# Revit family: Zumtobel MIRLRO NIV M600Q
name_source: partatom
category: Leuchten
revit_build: Autodesk Revit 2016 (Build: 20150714_1515(x64)
units: mm (PartAtom-declared; Revit-internal decimal feet)

## family parameters
Basisbauteil = Fläche
Beim Laden mit Abzugskörper schneiden = Nein
Bemaßung runder Anschluss = Durchmesser verwenden
Gemeinsam genutzt = Nein
Lichtquelle = Ja
OmniClass-Nummer = 23.80.70.11
OmniClass-Titel = Luminaries for Internal Lighting
Raumberechnungspunkt = Nein
Teiletyp = Normal

## types (2) — shared parameters
Baugruppenkennzeichen = D5020200
Beschreibung = Ceiling-recessed LED luminaire - levelling-in
Body = Zumtobel_Metal_White
Datei für fotometrisches Netz = D33416AA_MIREL_O_35W_LED840_M625Q.IES
Emissionsform beim Rendern sichtbar = Ja
Exterior Cover = Zumtobel_MIREL_Lamp_Self_llumination
Farbfilter = 16777215
Farbtemperaturverschiebung bei Dämpfen der Lampe = <Keine Auswahl>
Height = 85 mm  [stored 0.278871 ft]
Hersteller = Zumtobel Lighting
Interior Cover = Zumtobel_MIREL_Lamp_Self_llumination_Opaque
Lampe = LED
Length = 598 mm  [stored 1.96194 ft]
Neigungswinkel = 90.00°
Scheinlast = 37 VA
URL = http://www.zumtobel.com
Voltage = 230 V
Von Breite des Rechtecks ausssenden = 574 mm  [stored 1.8832 ft]
Von Länge des Rechtecks aussenden = 574 mm  [stored 1.8832 ft]
Width = 598 mm  [stored 1.96194 ft]
zero-valued in all types: Vorgabe-Ansicht

## per-type parameters (varying)
| type | Modell |
| MIRLRO NIV LED3800 LDO | 42185459 |
| MIRLRO NIV LED3800 EVG | 42182368 |

note: [stored X ft] marks values corroborated as IEEE doubles in the binary element streams (Revit-internal decimal feet)

## geometry (parser evidence)
native form markers: Blend x8, Sweep x3
no freeform markers — native parametric forms only
